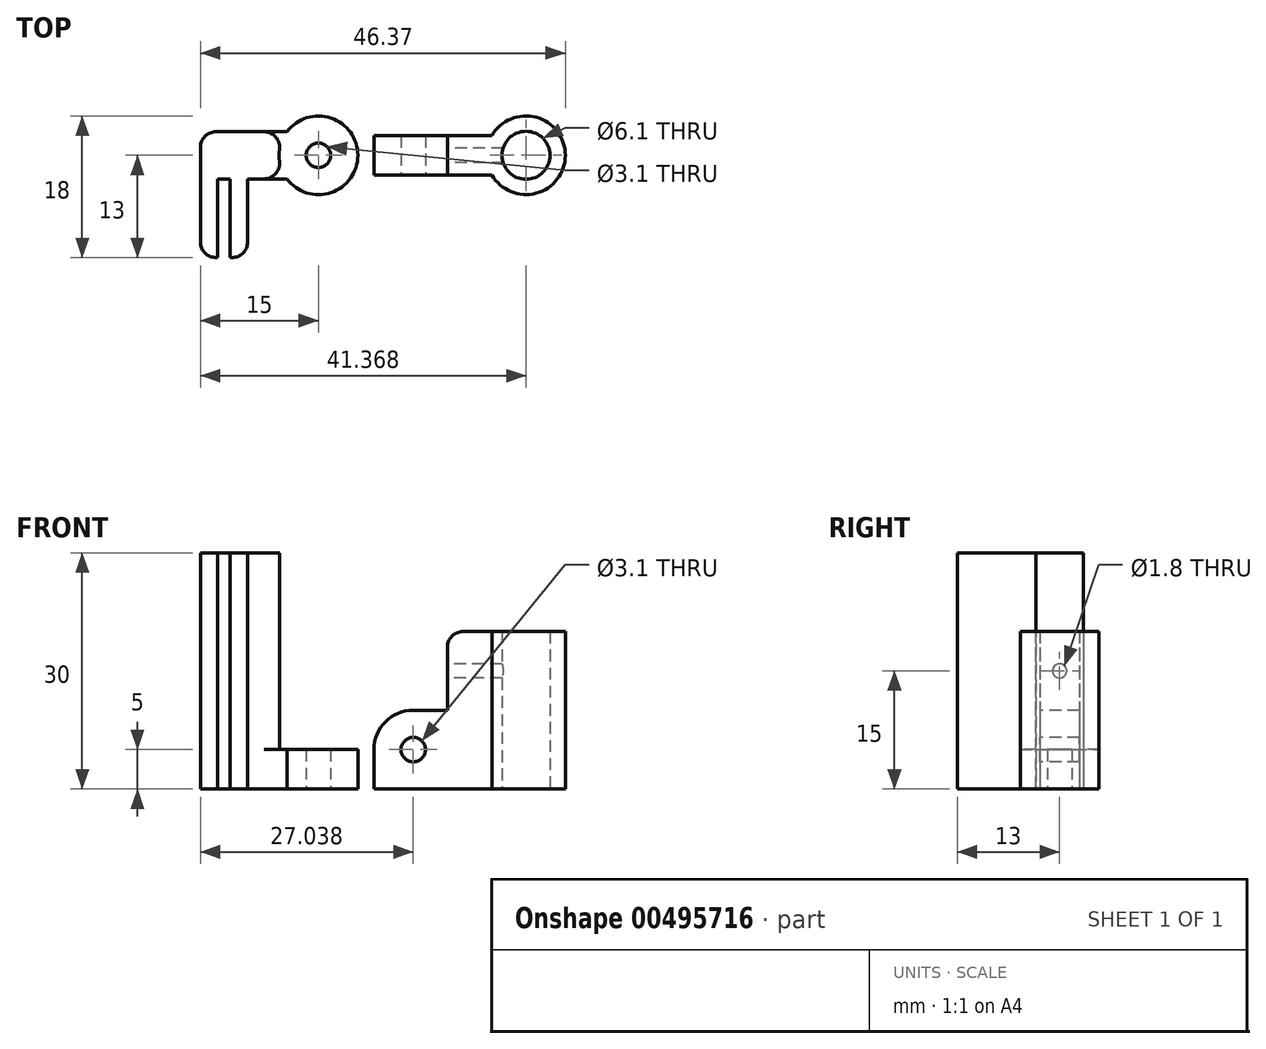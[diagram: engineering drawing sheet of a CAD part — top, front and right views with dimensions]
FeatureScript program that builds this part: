
annotation { "Feature Type Name" : "Feature", "Feature Type Description" : "" }
export const myFeature = defineFeature(function(context is Context, id is Id, definition is map)
    precondition{}
    {
        {
            var Q0;
            Q0=qCreatedBy(makeId("Top.planeOp"),FACE);
            var sketch = newSketch(context, id + "F0", { "sketchPlane" : qUnion([Q0])});
            skCircle(sketch, "E0", {"center": v(0, 0) * mm, "radius": 5 * mm});
            skLineSegment(sketch, "E1", {"start": v(0, 0) * mm, "end": v(-12, 0) * mm, "construction": true});
            skLineSegment(sketch, "E2", {"start": v(-12, 0) * mm, "end": v(-12, -13) * mm, "construction": true});
            skLineSegment(sketch, "E3", {"start": v(-15, -13) * mm, "end": v(-15, 3) * mm});
            skLineSegment(sketch, "E4", {"start": v(-15, 3) * mm, "end": v(-4, 3) * mm});
            skLineSegment(sketch, "E5", {"start": v(-9, -13) * mm, "end": v(-9, -3) * mm});
            skLineSegment(sketch, "E6", {"start": v(-9, -3) * mm, "end": v(-4, -3) * mm});
            skCircle(sketch, "E7", {"center": v(0, 0) * mm, "radius": 1.55 * mm});
            skLineSegment(sketch, "E8", {"start": v(-9, -3) * mm, "end": v(-15, -3) * mm, "construction": true});
            skLineSegment(sketch, "E9", {"start": v(-15, -13) * mm, "end": v(-12.8, -13) * mm});
            skLineSegment(sketch, "E10", {"start": v(-12.8, -13) * mm, "end": v(-12.8, -3) * mm});
            skLineSegment(sketch, "E11", {"start": v(-12.8, -3) * mm, "end": v(-11.2, -3) * mm});
            skLineSegment(sketch, "E12", {"start": v(-11.2, -3) * mm, "end": v(-11.2, -13) * mm});
            skLineSegment(sketch, "E13", {"start": v(-11.2, -13) * mm, "end": v(-9, -13) * mm});
            skSolve(sketch);
        }
        {
            var Q0;
            Q0=makeQuery(id+"F0.imprint","IMPRINT",FACE,{"disambiguationData":[TD([[makeQuery(id+"F0.imprint","IMPRINT",EDGE,{"derivedFrom":sQuery(id+"F0.wireOp",EDGE,"E7")}),-1.0]])]});
            extrude(context, id + "F1", {"entities" : qUnion([Q0]), "depth" : 5 * mm, "offsetDistance" : 25 * mm});
        }
        {
            var Q0;
            Q0=makeQuery(id+"F0.imprint","IMPRINT",FACE,{"disambiguationData":[TD([[makeQuery(id+"F0.imprint","IMPRINT",EDGE,{"derivedFrom":sQuery(id+"F0.wireOp",EDGE,"E3")}),-1.0]])]});
            extrude(context, id + "F2", {"entities" : qUnion([Q0]), "operationType" : NewBodyOperationType.ADD, "depth" : 30 * mm, "offsetDistance" : 25 * mm});
        }
        {
            var Q0;
            {var subQ0=sQuery(id+"F0.wireOp",EDGE,"E0");var subQ1=sQuery(id+"F0.wireOp",EDGE,"E4");Q0=makeQuery(id+"F2.boolean.opBoolean","SPLIT",EDGE,{"disambiguationData":[topologyDisambiguationEdgeConnected([makeQuery(id+"F2.opExtrude","SWEPT_FACE",FACE,{"disambiguationData":[OSD([subQ0])]})])],"derivedFrom":makeQuery(id+"F2.opExtrude","SWEPT_EDGE",EDGE,{"disambiguationData":[OSD([subQ0,subQ1])]})});}
            var Q1;
            {var subQ0=sQuery(id+"F0.wireOp",EDGE,"E0");var subQ1=sQuery(id+"F0.wireOp",EDGE,"E6");Q1=makeQuery(id+"F2.boolean.opBoolean","SPLIT",EDGE,{"disambiguationData":[topologyDisambiguationEdgeConnected([makeQuery(id+"F2.opExtrude","SWEPT_FACE",FACE,{"disambiguationData":[OSD([subQ0])]})])],"derivedFrom":makeQuery(id+"F2.opExtrude","SWEPT_EDGE",EDGE,{"disambiguationData":[OSD([subQ0,subQ1])]})});}
            var Q2;
            Q2=makeQuery(id+"F2.opExtrude","SWEPT_EDGE",EDGE,{"disambiguationData":[OSD([sQuery(id+"F0.wireOp",EDGE,"E3"),sQuery(id+"F0.wireOp",EDGE,"E4")])]});
            var Q3;
            Q3=makeQuery(id+"F2.opExtrude","SWEPT_EDGE",EDGE,{"disambiguationData":[OSD([sQuery(id+"F0.wireOp",EDGE,"E5"),sQuery(id+"F0.wireOp",EDGE,"E13")])]});
            var Q4;
            Q4=makeQuery(id+"F2.opExtrude","SWEPT_EDGE",EDGE,{"disambiguationData":[OSD([sQuery(id+"F0.wireOp",EDGE,"E3"),sQuery(id+"F0.wireOp",EDGE,"E9")])]});
            fillet(context, id + "F3", {"entities" : qUnion([Q0, Q1, Q2, Q3, Q4]), "radius" : 2 * mm, "tangentPropagation" : true, "allowEdgeOverflow" : false});
        }
        {
            var Q0;
            Q0=qCreatedBy(makeId("Top.planeOp"),FACE);
            var sketch = newSketch(context, id + "F4", { "sketchPlane" : qUnion([Q0]), "disableImprinting" : false});
            skCircle(sketch, "E14", {"center": v(26.37, 0) * mm, "radius": 3.05 * mm});
            skCircle(sketch, "E15", {"center": v(26.37, 0) * mm, "radius": 5 * mm});
            skLineSegment(sketch, "E16.bottom", {"start": v(22.04, -2.5) * mm, "end": v(7.04, -2.5) * mm});
            skLineSegment(sketch, "E16.top", {"start": v(22.04, 2.5) * mm, "end": v(7.04, 2.5) * mm});
            skLineSegment(sketch, "E16.right", {"start": v(7.04, -2.5) * mm, "end": v(7.04, 2.5) * mm});
            skPoint(sketch, "E16.middle", {"position": v(14.54, 0) * mm});
            skSolve(sketch);
        }
        {
            var Q0;
            Q0=makeQuery(id+"F4.imprint","IMPRINT",FACE,{"disambiguationData":[TD([[makeQuery(id+"F4.imprint","IMPRINT",EDGE,{"derivedFrom":sQuery(id+"F4.wireOp",EDGE,"E14")}),-1.0]])]});
            extrude(context, id + "F5", {"entities" : qUnion([Q0]), "depth" : 20 * mm, "offsetDistance" : 25 * mm});
        }
        {
            var Q0;
            {var subQ0=sQuery(id+"F4.wireOp",EDGE,"E16.bottom");Q0=makeQuery(id+"F4.imprint","IMPRINT",FACE,{"disambiguationData":[TD([[makeQuery(id+"F4.imprint","IMPRINT",EDGE,{"derivedFrom":subQ0}),-1.0]])]});}
            extrude(context, id + "F6", {"entities" : qUnion([Q0]), "operationType" : NewBodyOperationType.ADD, "depth" : 10 * mm, "offsetDistance" : 25 * mm});
        }
        {
            var Q0;
            Q0=makeQuery(id+"F6.opExtrude","SWEPT_FACE",FACE,{"disambiguationData":[OSD([sQuery(id+"F4.wireOp",EDGE,"E16.bottom")])]});
            var sketch = newSketch(context, id + "F7", { "sketchPlane" : qUnion([Q0])});
            skPoint(sketch, "E17", {"position": v(12.04, 10) * mm});
            skPoint(sketch, "E18", {"position": v(7.04, 5) * mm});
            skCircle(sketch, "E19", {"center": v(12.04, 5) * mm, "radius": 5 * mm});
            skCircle(sketch, "E20", {"center": v(12.04, 5) * mm, "radius": 1.55 * mm});
            skSolve(sketch);
        }
        {
            var Q0;
            {var subQ0=sQuery(id+"F7.wireOp",EDGE,"E19");var subQ1=sQuery(id+"F4.wireOp",EDGE,"E16.bottom");var subQ4=makeQuery(id+"F6.opExtrude","CAP_EDGE",EDGE,{"disambiguationData":[OSD([subQ1])],"isStart":false});var subQ5=makeQuery(id+"F7.imprint","INTERSECT",VERTEX,{"derivedFrom":[subQ4,subQ0]});Q0=makeQuery(id+"F7.imprint","IMPRINT",FACE,{"disambiguationData":[TD([[makeQuery(id+"F7.imprint","IMPRINT",EDGE,{"disambiguationData":[TD([[subQ5,-1.0]])],"derivedFrom":subQ0}),-1.0]])]});}
            var Q1;
            Q1=makeQuery(id+"F7.imprint","IMPRINT",FACE,{"disambiguationData":[TD([[makeQuery(id+"F7.imprint","IMPRINT",EDGE,{"derivedFrom":sQuery(id+"F7.wireOp",EDGE,"E20")}),1.0]])]});
            extrude(context, id + "F8", {"entities" : qUnion([Q0, Q1]), "operationType" : NewBodyOperationType.REMOVE, "oppositeDirection" : true, "depth" : 25 * mm, "offsetDistance" : 25 * mm});
        }
        {
            var Q0;
            Q0=makeQuery(id+"F6.opExtrude","CAP_FACE",FACE,{"disambiguationData":[OSD([sQuery(id+"F4.wireOp",EDGE,"E15"),sQuery(id+"F4.wireOp",EDGE,"E16.bottom"),sQuery(id+"F4.wireOp",EDGE,"E16.top"),sQuery(id+"F4.wireOp",EDGE,"E16.right")])],"isStart":false});
            var sketch = newSketch(context, id + "F9", { "sketchPlane" : qUnion([Q0])});
            skLineSegment(sketch, "E21", {"start": v(16.37, 2.5) * mm, "end": v(16.37, -2.5) * mm});
            skSolve(sketch);
        }
        {
            var Q0;
            {var subQ0=sQuery(id+"F9.wireOp",EDGE,"E21");Q0=makeQuery(id+"F9.imprint","IMPRINT",FACE,{"disambiguationData":[TD([[makeQuery(id+"F9.imprint","IMPRINT",EDGE,{"derivedFrom":subQ0}),1.0]])]});}
            extrude(context, id + "F10", {"entities" : qUnion([Q0]), "operationType" : NewBodyOperationType.ADD, "depth" : 10 * mm, "offsetDistance" : 25 * mm});
        }
        {
            var Q0;
            Q0=makeQuery(id+"F10.opExtrude","SWEPT_FACE",FACE,{"disambiguationData":[OSD([sQuery(id+"F9.wireOp",EDGE,"E21")])]});
            var sketch = newSketch(context, id + "F11", { "sketchPlane" : qUnion([Q0])});
            skCircle(sketch, "E22", {"center": v(0, 15) * mm, "radius": 0.9 * mm});
            skPoint(sketch, "E22.centerSnap0", {"position": v(-2.5, 15) * mm});
            skSolve(sketch);
        }
        {
            var Q0;
            Q0=makeQuery(id+"F11.imprint","IMPRINT",FACE,{"disambiguationData":[TD([[makeQuery(id+"F11.imprint","IMPRINT",EDGE,{"derivedFrom":sQuery(id+"F11.wireOp",EDGE,"E22")}),1.0]])]});
            extrude(context, id + "F12", {"entities" : qUnion([Q0]), "operationType" : NewBodyOperationType.REMOVE, "oppositeDirection" : true, "depth" : 10 * mm, "offsetDistance" : 25 * mm});
        }
        {
            var Q0;
            Q0=makeQuery(id+"F10.opExtrude","CAP_EDGE",EDGE,{"disambiguationData":[OSD([sQuery(id+"F9.wireOp",EDGE,"E21")])],"isStart":false});
            var Q1;
            Q1=makeQuery(id+"F10.opExtrude","CAP_EDGE",EDGE,{"disambiguationData":[OSD([sQuery(id+"F9.wireOp",EDGE,"E21")])],"isStart":true});
            fillet(context, id + "F13", {"entities" : qUnion([Q0, Q1]), "radius" : 2 * mm, "tangentPropagation" : true, "allowEdgeOverflow" : false});
        }
    });
